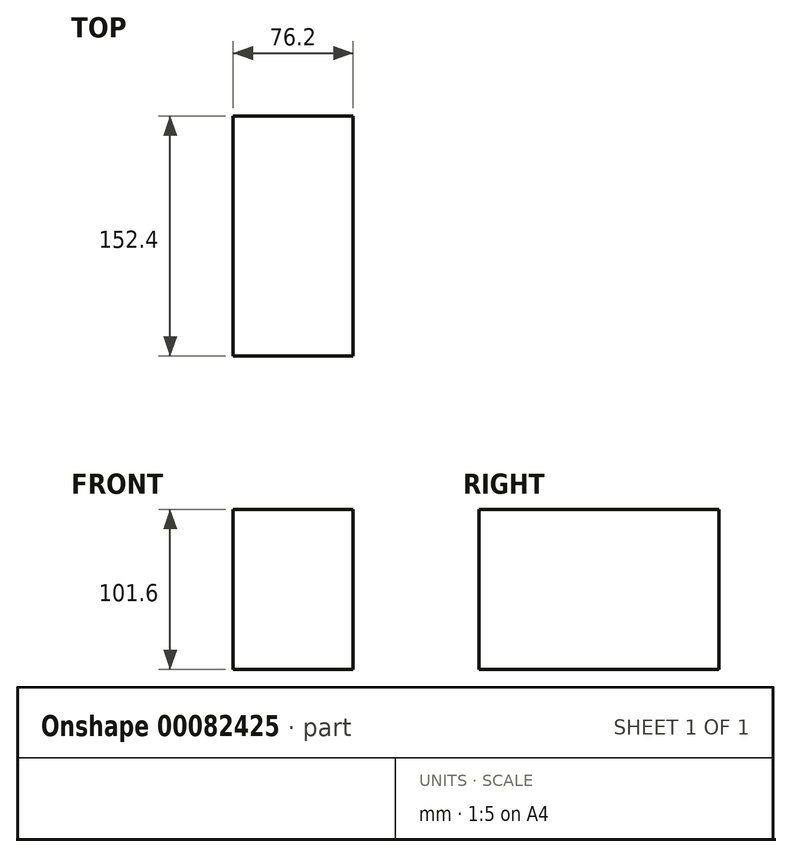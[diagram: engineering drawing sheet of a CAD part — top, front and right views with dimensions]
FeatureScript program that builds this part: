
annotation { "Feature Type Name" : "Feature", "Feature Type Description" : "" }
export const myFeature = defineFeature(function(context is Context, id is Id, definition is map)
    precondition{}
    {
        {
            var Q0;
            Q0=qCreatedBy(makeId("Right.planeOp"),FACE);
            var sketch = newSketch(context, id + "F0", { "sketchPlane" : qUnion([Q0])});
            skLineSegment(sketch, "E0.bottom", {"start": v(76.2, 50.8) * mm, "end": v(-76.2, 50.8) * mm});
            skLineSegment(sketch, "E0.top", {"start": v(76.2, -50.8) * mm, "end": v(-76.2, -50.8) * mm});
            skLineSegment(sketch, "E0.left", {"start": v(76.2, 50.8) * mm, "end": v(76.2, -50.8) * mm});
            skLineSegment(sketch, "E0.right", {"start": v(-76.2, 50.8) * mm, "end": v(-76.2, -50.8) * mm});
            skPoint(sketch, "E0.middle", {"position": v(0, 0) * mm});
            skSolve(sketch);
        }
        {
            var Q0;
            Q0 = qSketchRegion(id + "F0", true);
            extrude(context, id + "F1", {"entities" : qUnion([Q0]), "depth" : 76.2 * mm});
        }
    });
